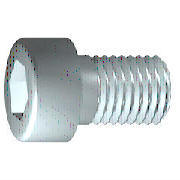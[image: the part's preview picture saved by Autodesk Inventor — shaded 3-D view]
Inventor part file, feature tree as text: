
AUTODESK INVENTOR PART (.ipt)
format: ipt  version: 2018 (Build 220112000, 112)  size: 182,272 bytes
history: native  units: mm (DEFAULTED — no unit token found)
features: sketch x2, extrude x1, plane x1, fillet x1
ambient origin geometry x7: Origin, YZ Plane, XY Plane, X Axis, Y Axis, Z Axis, Center Point
bodies: Solid1 (feature_tree), Body (feature_tree)
feature tree (5):
  extrude  "Slot"  Depth=3.0mm
  plane  "Work Plane1"
  fillet  "Fillet2"  Radius=3.0mm
  sketch  "Sketch1"  dims[d1=18.0mm d2=0.306825mm d3=3.0mm]
  sketch  "Sketch2"  dims[d4=1.5mm d5=60.0deg d6=3.0mm d7=3.0mm d8=2.886751mm d9=5.5mm d10=90.0deg d11=10.0mm d12=0.0mm d13=18.0mm d14=0.0mm d15=0.306725mm d16=0.306725mm d17=0.3mm d19=0.0mm d26=35.0mm d27=45.0deg d28=0.0mm d29=0.0mm d30=0.1mm]
